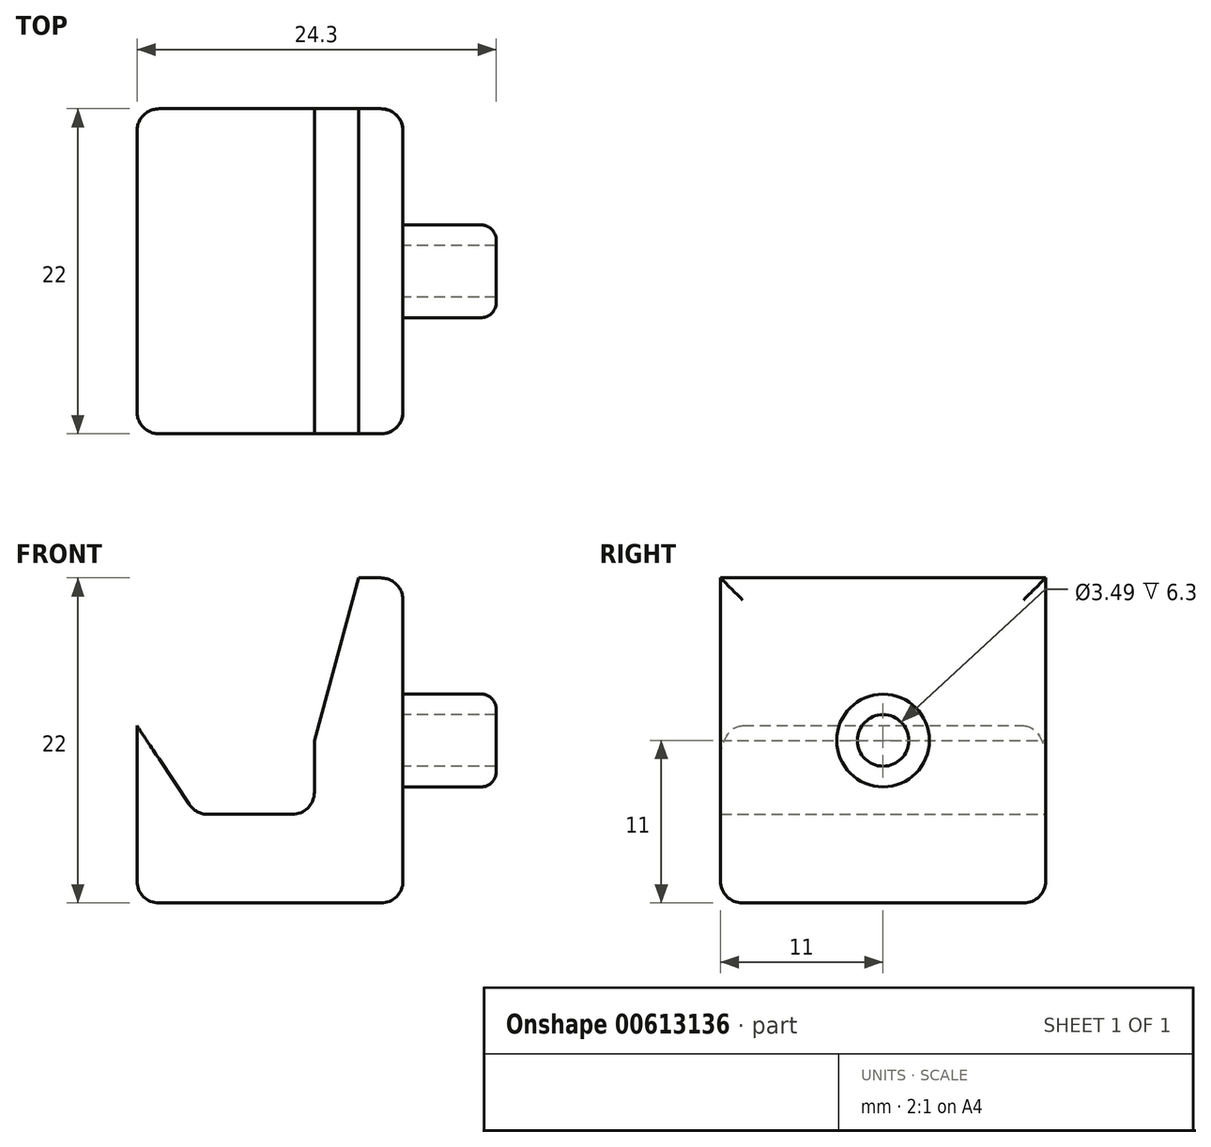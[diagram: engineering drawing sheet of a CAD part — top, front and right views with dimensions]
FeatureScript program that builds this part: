
annotation { "Feature Type Name" : "Feature", "Feature Type Description" : "" }
export const myFeature = defineFeature(function(context is Context, id is Id, definition is map)
    precondition{}
    {
        {
            var Q0;
            Q0=qCreatedBy(makeId("Front.planeOp"),FACE);
            var sketch = newSketch(context, id + "F0", { "sketchPlane" : qUnion([Q0])});
            skLineSegment(sketch, "E0.top", {"start": v(3, -11) * mm, "end": v(-3, -11) * mm});
            skLineSegment(sketch, "E0.left", {"start": v(3, 11) * mm, "end": v(3, -11) * mm});
            skPoint(sketch, "E0.middle", {"position": v(0, 0) * mm});
            skLineSegment(sketch, "E1.bottom", {"start": v(-3, -11) * mm, "end": v(-15, -11) * mm});
            skLineSegment(sketch, "E1.right", {"start": v(-15, -11) * mm, "end": v(-15, -5) * mm});
            skLineSegment(sketch, "E2", {"start": v(0, 11) * mm, "end": v(-3, 0) * mm});
            skLineSegment(sketch, "E3.left", {"start": v(-15, -5) * mm, "end": v(-15, 1) * mm});
            skLineSegment(sketch, "E4", {"start": v(-11, -5) * mm, "end": v(-15, 1) * mm});
            skLineSegment(sketch, "E5", {"start": v(-3, 0) * mm, "end": v(-3, -5) * mm});
            skLineSegment(sketch, "E6", {"start": v(3, 11) * mm, "end": v(0, 11) * mm});
            skLineSegment(sketch, "E7.top", {"start": v(3, 3.15) * mm, "end": v(9, 3.15) * mm});
            skLineSegment(sketch, "E7.left", {"start": v(3, 0) * mm, "end": v(3, 3.15) * mm});
            skLineSegment(sketch, "E7.right", {"start": v(9, 0) * mm, "end": v(9, 3.15) * mm});
            skLineSegment(sketch, "E8.top", {"start": v(3, -3.2) * mm, "end": v(9, -3.2) * mm});
            skLineSegment(sketch, "E8.left", {"start": v(3, 0) * mm, "end": v(3, -3.2) * mm});
            skLineSegment(sketch, "E8.right", {"start": v(9, 0) * mm, "end": v(9, -3.2) * mm});
            skLineSegment(sketch, "E9", {"start": v(-11, -5) * mm, "end": v(-3, -5) * mm});
            skSolve(sketch);
        }
        {
            var Q0;
            {var subQ1=sQuery(id+"F0.wireOp",EDGE,"E0.top");Q0=makeQuery(id+"F0.imprint","IMPRINT",FACE,{"disambiguationData":[TD([[makeQuery(id+"F0.imprint","IMPRINT",EDGE,{"derivedFrom":subQ1}),-1.0]])]});}
            extrude(context, id + "F1", {"entities" : qUnion([Q0]), "depth" : 11 * mm, "offsetDistance" : 25 * mm, "hasSecondDirection" : true, "secondDirectionOppositeDirection" : true, "secondDirectionDepth" : 11 * mm});
        }
        {
            var Q0;
            Q0=makeQuery(id+"F1.opExtrude","SWEPT_FACE",FACE,{"disambiguationData":[OSD([sQuery(id+"F0.wireOp",EDGE,"E0.left"),sQuery(id+"F0.wireOp",EDGE,"E7.left"),sQuery(id+"F0.wireOp",EDGE,"E8.left")])]});
            var sketch = newSketch(context, id + "F2", { "sketchPlane" : qUnion([Q0])});
            skCircle(sketch, "E10", {"center": v(0, 0) * mm, "radius": 3.14 * mm});
            skCircle(sketch, "E11", {"center": v(0, 0) * mm, "radius": 1.74 * mm});
            skSolve(sketch);
        }
        {
            var Q0;
            Q0=makeQuery(id+"F2.imprint","IMPRINT",FACE,{"disambiguationData":[TD([[makeQuery(id+"F2.imprint","IMPRINT",EDGE,{"derivedFrom":sQuery(id+"F2.wireOp",EDGE,"E10")}),1.0]])]});
            extrude(context, id + "F3", {"entities" : qUnion([Q0]), "operationType" : NewBodyOperationType.ADD, "depth" : 6.3 * mm, "offsetDistance" : 25 * mm});
        }
        {
            var Q0;
            Q0=makeQuery(id+"F1.opExtrude","CAP_EDGE",EDGE,{"disambiguationData":[OSD([sQuery(id+"F0.wireOp",EDGE,"E0.left"),sQuery(id+"F0.wireOp",EDGE,"E7.left"),sQuery(id+"F0.wireOp",EDGE,"E8.left")])],"isStart":false});
            var Q1;
            Q1=makeQuery(id+"F1.opExtrude","CAP_EDGE",EDGE,{"disambiguationData":[OSD([sQuery(id+"F0.wireOp",EDGE,"E0.top"),sQuery(id+"F0.wireOp",EDGE,"E1.bottom")])],"isStart":false});
            var Q2;
            Q2=makeQuery(id+"F1.opExtrude","CAP_EDGE",EDGE,{"disambiguationData":[OSD([sQuery(id+"F0.wireOp",EDGE,"E1.right"),sQuery(id+"F0.wireOp",EDGE,"E3.left")])],"isStart":false});
            var Q3;
            Q3=makeQuery(id+"F1.opExtrude","SWEPT_EDGE",EDGE,{"disambiguationData":[OSD([sQuery(id+"F0.wireOp",EDGE,"E0.left"),sQuery(id+"F0.wireOp",EDGE,"E6")])]});
            var Q4;
            Q4=makeQuery(id+"F1.opExtrude","CAP_EDGE",EDGE,{"disambiguationData":[OSD([sQuery(id+"F0.wireOp",EDGE,"E0.left"),sQuery(id+"F0.wireOp",EDGE,"E7.left"),sQuery(id+"F0.wireOp",EDGE,"E8.left")])],"isStart":true});
            var Q5;
            Q5=makeQuery(id+"F1.opExtrude","SWEPT_EDGE",EDGE,{"disambiguationData":[OSD([sQuery(id+"F0.wireOp",EDGE,"E0.top"),sQuery(id+"F0.wireOp",EDGE,"E0.left")])]});
            var Q6;
            Q6=makeQuery(id+"F1.opExtrude","CAP_EDGE",EDGE,{"disambiguationData":[OSD([sQuery(id+"F0.wireOp",EDGE,"E1.right"),sQuery(id+"F0.wireOp",EDGE,"E3.left")])],"isStart":true});
            var Q7;
            Q7=makeQuery(id+"F1.opExtrude","SWEPT_EDGE",EDGE,{"disambiguationData":[OSD([sQuery(id+"F0.wireOp",EDGE,"E1.bottom"),sQuery(id+"F0.wireOp",EDGE,"E1.right")])]});
            var Q8;
            Q8=makeQuery(id+"F1.opExtrude","CAP_EDGE",EDGE,{"disambiguationData":[OSD([sQuery(id+"F0.wireOp",EDGE,"E0.top"),sQuery(id+"F0.wireOp",EDGE,"E1.bottom")])],"isStart":true});
            var Q9;
            Q9=makeQuery(id+"F1.opExtrude","SWEPT_EDGE",EDGE,{"disambiguationData":[OSD([sQuery(id+"F0.wireOp",EDGE,"E5"),sQuery(id+"F0.wireOp",EDGE,"E9")])]});
            var Q10;
            Q10=makeQuery(id+"F1.opExtrude","SWEPT_EDGE",EDGE,{"disambiguationData":[OSD([sQuery(id+"F0.wireOp",EDGE,"E4"),sQuery(id+"F0.wireOp",EDGE,"E9")])]});
            fillet(context, id + "F4", {"entities" : qUnion([Q0, Q1, Q2, Q3, Q4, Q5, Q6, Q7, Q8, Q9, Q10]), "radius" : 1.5 * mm, "tangentPropagation" : true, "allowEdgeOverflow" : false});
        }
        {
            var Q0;
            Q0=makeQuery(id+"F3.opExtrude","CAP_EDGE",EDGE,{"disambiguationData":[OSD([sQuery(id+"F2.wireOp",EDGE,"E10")])],"isStart":false});
            fillet(context, id + "F5", {"entities" : qUnion([Q0]), "radius" : 1 * mm, "tangentPropagation" : true, "allowEdgeOverflow" : false});
        }
        {
            var Q0;
            Q0=makeQuery(id+"F3.boolean.opBoolean","SPLIT",FACE,{"disambiguationData":[TD([makeQuery(id+"F3.opExtrude","SWEPT_FACE",FACE,{"disambiguationData":[OSD([sQuery(id+"F2.wireOp",EDGE,"E11")])]})])],"derivedFrom":makeQuery(id+"F1.opExtrude","SWEPT_FACE",FACE,{"disambiguationData":[OSD([sQuery(id+"F0.wireOp",EDGE,"E0.left"),sQuery(id+"F0.wireOp",EDGE,"E7.left"),sQuery(id+"F0.wireOp",EDGE,"E8.left")])]})});
            extrude(context, id + "F6", {"entities" : qUnion([Q0]), "operationType" : NewBodyOperationType.ADD, "oppositeDirection" : true, "depth" : 1.5 * mm, "offsetDistance" : 25 * mm});
        }
    });
